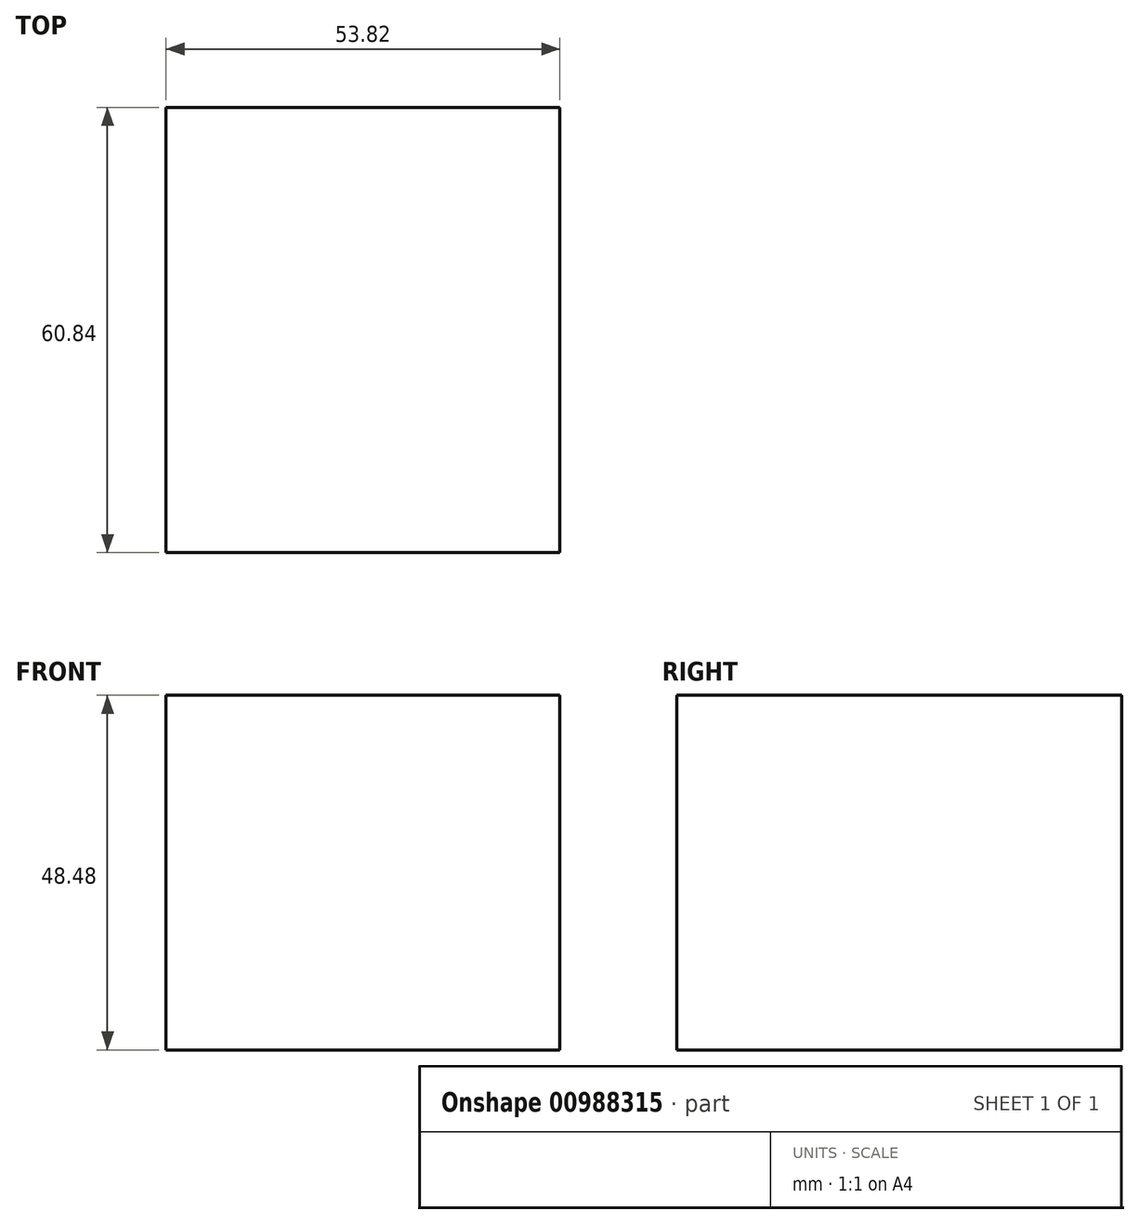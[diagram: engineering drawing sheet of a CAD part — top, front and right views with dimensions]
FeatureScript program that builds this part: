
annotation { "Feature Type Name" : "Feature", "Feature Type Description" : "" }
export const myFeature = defineFeature(function(context is Context, id is Id, definition is map)
    precondition{}
    {
        {
            var Q0;
            Q0=qCreatedBy(makeId("Top.planeOp"),FACE);
            var sketch = newSketch(context, id + "F0", { "sketchPlane" : qUnion([Q0])});
            skLineSegment(sketch, "E0.bottom", {"start": v(26.91, -30.42) * mm, "end": v(-26.91, -30.42) * mm});
            skLineSegment(sketch, "E0.top", {"start": v(26.91, 30.42) * mm, "end": v(-26.91, 30.42) * mm});
            skLineSegment(sketch, "E0.left", {"start": v(26.91, -30.42) * mm, "end": v(26.91, 30.42) * mm});
            skLineSegment(sketch, "E0.right", {"start": v(-26.91, -30.42) * mm, "end": v(-26.91, 30.42) * mm});
            skPoint(sketch, "E0.middle", {"position": v(0, 0) * mm});
            skSolve(sketch);
        }
        {
            var Q0;
            Q0=makeQuery(id+"F0.imprint","IMPRINT",FACE,{"disambiguationData":[TD([[makeQuery(id+"F0.imprint","IMPRINT",EDGE,{"derivedFrom":sQuery(id+"F0.wireOp",EDGE,"E0.bottom")}),-1.0]])]});
            extrude(context, id + "F1", {"entities" : qUnion([Q0]), "depth" : 48.48 * mm, "offsetDistance" : 25.4 * mm});
        }
    });
